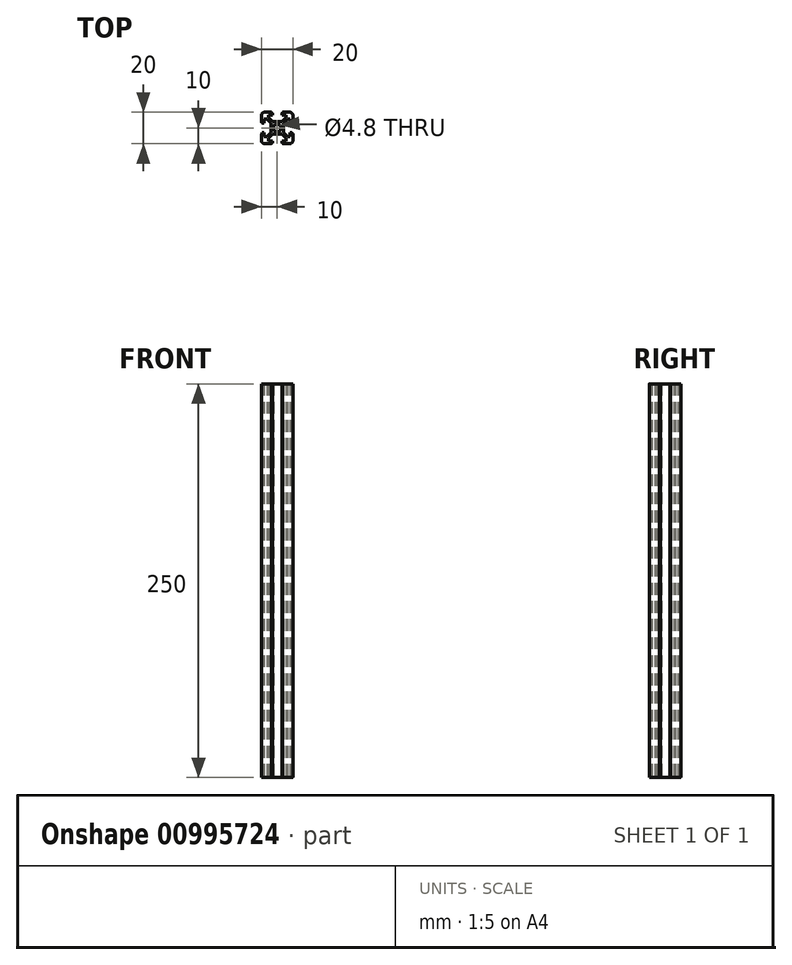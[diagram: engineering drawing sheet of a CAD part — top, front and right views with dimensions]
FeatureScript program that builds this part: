
annotation { "Feature Type Name" : "Feature", "Feature Type Description" : "" }
export const myFeature = defineFeature(function(context is Context, id is Id, definition is map)
    precondition{}
    {
        {
            var Q0;
            Q0=qCreatedBy(makeId("Top.planeOp"),FACE);
            var sketch = newSketch(context, id + "F0", { "sketchPlane" : qUnion([Q0])});
            skLineSegment(sketch, "E0.bottom", {"start": v(10, 10) * mm, "end": v(3.5, 10) * mm});
            skLineSegment(sketch, "E0.top", {"start": v(10, -10) * mm, "end": v(3.5, -10) * mm});
            skLineSegment(sketch, "E0.left", {"start": v(10, 10) * mm, "end": v(10, 3.5) * mm});
            skLineSegment(sketch, "E0.right", {"start": v(-10, 10) * mm, "end": v(-10, 3.5) * mm});
            skPoint(sketch, "E0.middle", {"position": v(0, 0) * mm});
            skLineSegment(sketch, "E1", {"start": v(3.5, 10) * mm, "end": v(3.5, 9.5) * mm});
            skLineSegment(sketch, "E2", {"start": v(3.5, 9.5) * mm, "end": v(3, 9.5) * mm});
            skLineSegment(sketch, "E3", {"start": v(3, 9.5) * mm, "end": v(3, 8.2) * mm});
            skLineSegment(sketch, "E4", {"start": v(3, 8.2) * mm, "end": v(5.5, 8.2) * mm});
            skLineSegment(sketch, "E5", {"start": v(5.5, 8.2) * mm, "end": v(5.5, 6.56) * mm});
            skLineSegment(sketch, "E6", {"start": v(5.5, 6.56) * mm, "end": v(2.94, 4) * mm});
            skLineSegment(sketch, "E7", {"start": v(2.94, 4) * mm, "end": v(0, 4) * mm});
            skLineSegment(sketch, "E8", {"start": v(10, 10) * mm, "end": v(0, 0) * mm, "construction": true});
            skLineSegment(sketch, "E9", {"start": v(0, 10) * mm, "end": v(0, -10) * mm, "construction": true});
            skLineSegment(sketch, "E10", {"start": v(10, 0) * mm, "end": v(-10, 0) * mm, "construction": true});
            skLineSegment(sketch, "E11.MirrorCS", {"start": v(-2.94, 4) * mm, "end": v(0, 4) * mm});
            skLineSegment(sketch, "E12.MirrorCS", {"start": v(10, 3.5) * mm, "end": v(9.5, 3.5) * mm});
            skLineSegment(sketch, "E13.MirrorCS", {"start": v(9.5, 3.5) * mm, "end": v(9.5, 3) * mm});
            skLineSegment(sketch, "E14.MirrorCS", {"start": v(8.2, 5.5) * mm, "end": v(6.56, 5.5) * mm});
            skLineSegment(sketch, "E15.MirrorCS", {"start": v(9.5, 3) * mm, "end": v(8.2, 3) * mm});
            skLineSegment(sketch, "E16.MirrorCS", {"start": v(8.2, 3) * mm, "end": v(8.2, 5.5) * mm});
            skLineSegment(sketch, "E17.MirrorCS", {"start": v(6.56, 5.5) * mm, "end": v(4, 2.94) * mm});
            skLineSegment(sketch, "E18.MirrorCS", {"start": v(-3.5, 9.5) * mm, "end": v(-3, 9.5) * mm});
            skLineSegment(sketch, "E19.MirrorCS", {"start": v(-9.5, 3) * mm, "end": v(-8.2, 3) * mm});
            skLineSegment(sketch, "E20.MirrorCS", {"start": v(-3.5, 10) * mm, "end": v(-3.5, 9.5) * mm});
            skLineSegment(sketch, "E21.MirrorCS", {"start": v(-8.2, 5.5) * mm, "end": v(-6.56, 5.5) * mm});
            skLineSegment(sketch, "E22.MirrorCS", {"start": v(-9.5, 3.5) * mm, "end": v(-9.5, 3) * mm});
            skLineSegment(sketch, "E23.MirrorCS", {"start": v(-10, 3.5) * mm, "end": v(-9.5, 3.5) * mm});
            skLineSegment(sketch, "E24.MirrorCS", {"start": v(-5.5, 8.2) * mm, "end": v(-5.5, 6.56) * mm});
            skLineSegment(sketch, "E25.MirrorCS", {"start": v(-3, 9.5) * mm, "end": v(-3, 8.2) * mm});
            skLineSegment(sketch, "E26.MirrorCS", {"start": v(-3, 8.2) * mm, "end": v(-5.5, 8.2) * mm});
            skLineSegment(sketch, "E27.MirrorCS", {"start": v(-10, 10) * mm, "end": v(-3.5, 10) * mm});
            skLineSegment(sketch, "E28.MirrorCS", {"start": v(-6.56, 5.5) * mm, "end": v(-4, 2.94) * mm});
            skLineSegment(sketch, "E29.MirrorCS", {"start": v(-5.5, 6.56) * mm, "end": v(-2.94, 4) * mm});
            skLineSegment(sketch, "E30.MirrorCS", {"start": v(-8.2, 3) * mm, "end": v(-8.2, 5.5) * mm});
            skLineSegment(sketch, "E31.MirrorCS", {"start": v(-3.5, -10) * mm, "end": v(-3.5, -9.5) * mm});
            skLineSegment(sketch, "E32.MirrorCS", {"start": v(-3.5, -9.5) * mm, "end": v(-3, -9.5) * mm});
            skLineSegment(sketch, "E33.MirrorCS", {"start": v(5.5, -8.2) * mm, "end": v(5.5, -6.56) * mm});
            skLineSegment(sketch, "E34.MirrorCS", {"start": v(3, -8.2) * mm, "end": v(5.5, -8.2) * mm});
            skLineSegment(sketch, "E35.MirrorCS", {"start": v(-3, -9.5) * mm, "end": v(-3, -8.2) * mm});
            skLineSegment(sketch, "E36.MirrorCS", {"start": v(3, -9.5) * mm, "end": v(3, -8.2) * mm});
            skLineSegment(sketch, "E37.MirrorCS", {"start": v(10, -3.5) * mm, "end": v(9.5, -3.5) * mm});
            skLineSegment(sketch, "E38.MirrorCS", {"start": v(3.5, -10) * mm, "end": v(3.5, -9.5) * mm});
            skLineSegment(sketch, "E39.MirrorCS", {"start": v(3.5, -9.5) * mm, "end": v(3, -9.5) * mm});
            skLineSegment(sketch, "E40.MirrorCS", {"start": v(-8.2, -5.5) * mm, "end": v(-6.56, -5.5) * mm});
            skLineSegment(sketch, "E41.MirrorCS", {"start": v(9.5, -3.5) * mm, "end": v(9.5, -3) * mm});
            skLineSegment(sketch, "E42.MirrorCS", {"start": v(-9.5, -3.5) * mm, "end": v(-9.5, -3) * mm});
            skLineSegment(sketch, "E43.MirrorCS", {"start": v(-3, -8.2) * mm, "end": v(-5.5, -8.2) * mm});
            skLineSegment(sketch, "E44.MirrorCS", {"start": v(-5.5, -8.2) * mm, "end": v(-5.5, -6.56) * mm});
            skLineSegment(sketch, "E45.MirrorCS", {"start": v(-9.5, -3) * mm, "end": v(-8.2, -3) * mm});
            skLineSegment(sketch, "E46.MirrorCS", {"start": v(8.2, -5.5) * mm, "end": v(6.56, -5.5) * mm});
            skLineSegment(sketch, "E47.MirrorCS", {"start": v(9.5, -3) * mm, "end": v(8.2, -3) * mm});
            skLineSegment(sketch, "E48.MirrorCS", {"start": v(-10, -3.5) * mm, "end": v(-9.5, -3.5) * mm});
            skLineSegment(sketch, "E49.MirrorCS", {"start": v(8.2, -3) * mm, "end": v(8.2, -5.5) * mm});
            skLineSegment(sketch, "E50.MirrorCS", {"start": v(6.56, -5.5) * mm, "end": v(4, -2.94) * mm});
            skLineSegment(sketch, "E51.MirrorCS", {"start": v(2.94, -4) * mm, "end": v(0, -4) * mm});
            skLineSegment(sketch, "E52.MirrorCS", {"start": v(-10, -10) * mm, "end": v(-3.5, -10) * mm});
            skLineSegment(sketch, "E53.MirrorCS", {"start": v(-6.56, -5.5) * mm, "end": v(-4, -2.94) * mm});
            skLineSegment(sketch, "E54.MirrorCS", {"start": v(5.5, -6.56) * mm, "end": v(2.94, -4) * mm});
            skLineSegment(sketch, "E55.MirrorCS", {"start": v(-5.5, -6.56) * mm, "end": v(-2.94, -4) * mm});
            skLineSegment(sketch, "E56.MirrorCS", {"start": v(-8.2, -3) * mm, "end": v(-8.2, -5.5) * mm});
            skLineSegment(sketch, "E57.MirrorCS", {"start": v(-2.94, -4) * mm, "end": v(0, -4) * mm});
            skLineSegment(sketch, "E58", {"start": v(-4, 2.94) * mm, "end": v(-4, -2.94) * mm});
            skLineSegment(sketch, "E59", {"start": v(4, 2.94) * mm, "end": v(4, -2.94) * mm});
            skCircle(sketch, "E60", {"center": v(0, 0) * mm, "radius": 2.4 * mm});
            skLineSegment(sketch, "E61.trimOffspring", {"start": v(-3.5, -10) * mm, "end": v(-10, -10) * mm});
            skLineSegment(sketch, "E62.trimOffspring", {"start": v(10, -3.5) * mm, "end": v(10, -10) * mm});
            skLineSegment(sketch, "E63.trimOffspring", {"start": v(-10, -3.5) * mm, "end": v(-10, -10) * mm});
            skSolve(sketch);
        }
        {
            var Q0;
            Q0=qSketchRegion(id+"F0",true);
            extrude(context, id + "F1", {"entities" : qUnion([Q0]), "depth" : 250 * mm, "offsetDistance" : 25 * mm});
        }
        {
            var Q0;
            Q0=makeQuery(id+"F1.opExtrude","SWEPT_EDGE",EDGE,{"disambiguationData":[OSD([sQuery(id+"F0.wireOp",EDGE,"E0.bottom"),sQuery(id+"F0.wireOp",EDGE,"E0.left")])]});
            var Q1;
            Q1=makeQuery(id+"F1.opExtrude","SWEPT_EDGE",EDGE,{"disambiguationData":[OSD([sQuery(id+"F0.wireOp",EDGE,"E0.top"),sQuery(id+"F0.wireOp",EDGE,"E62.trimOffspring")])]});
            var Q2;
            Q2=makeQuery(id+"F1.opExtrude","SWEPT_EDGE",EDGE,{"disambiguationData":[OSD([sQuery(id+"F0.wireOp",EDGE,"E61.trimOffspring"),sQuery(id+"F0.wireOp",EDGE,"E63.trimOffspring")])]});
            var Q3;
            Q3=makeQuery(id+"F1.opExtrude","SWEPT_EDGE",EDGE,{"disambiguationData":[OSD([sQuery(id+"F0.wireOp",EDGE,"E0.right"),sQuery(id+"F0.wireOp",EDGE,"E27.MirrorCS")])]});
            fillet(context, id + "F2", {"entities" : qUnion([Q0, Q1, Q2, Q3]), "radius" : 2 * mm, "tangentPropagation" : true, "allowEdgeOverflow" : false});
        }
    });
